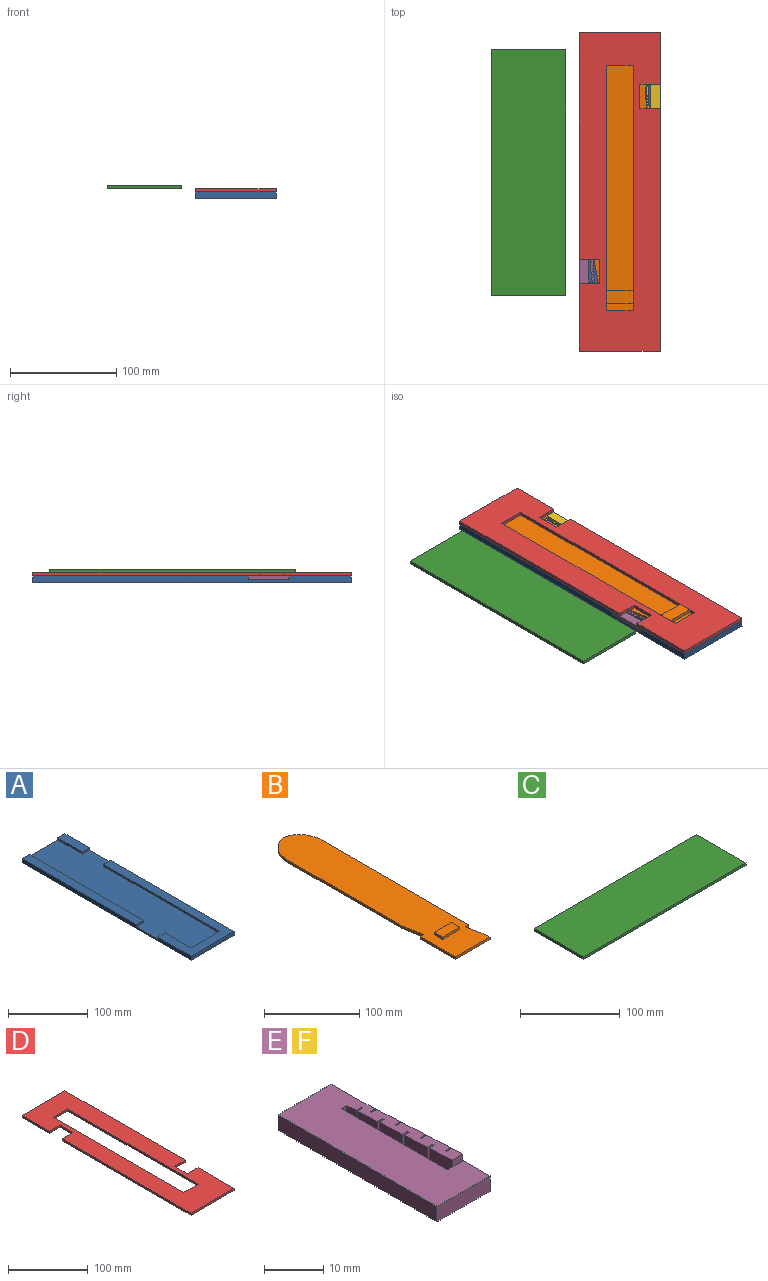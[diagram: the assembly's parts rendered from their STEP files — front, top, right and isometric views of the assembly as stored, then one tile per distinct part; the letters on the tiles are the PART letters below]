
ASSEMBLY  parts=6 mates=5
PART A: 18 faces, bbox 76.2x299.7x6.4 mm
  f0: plane 43.39x12.7mm, normal (0,0,1), area 551.1mm2, adj f7,f9,f16,f17
  f1: plane 205.53x3.18mm, normal (-1,0,0), area 652.6mm2, adj f3,f6,f10,f15
  f2: plane 202.95x3.18mm, normal (1,0,0), area 644.4mm2, adj f6,f12,f13,f17
  f3: plane 218.23x76.2mm, normal (0,0,1), area 4161.8mm2, adj f1,f4,f5,f7,f10,f11,f14,f15
  f4: plane 299.72x6.35mm, normal (-1,0,0), area 1782.3mm2, adj f3,f5,f6,f8,f12,f13,f14,f17
  f5: plane 76.2x6.35mm, normal (0,-1,0), area 483.9mm2, adj f3,f4,f7,f8
  f6: plane 287.02x76.2mm, normal (0,0,1), area 15548.4mm2, adj f1,f2,f4,f7,f9,f10,f11,f13
  f7: plane 299.72x6.35mm, normal (1,0,0), area 1782.3mm2, adj f0,f3,f5,f6,f8,f15,f16,f17
  f8: plane 299.72x76.2mm, normal (0,0,-1), area 22838.7mm2, adj f4,f5,f7,f17
  f9: plane 43.39x3.18mm, normal (-1,0,0), area 137.8mm2, adj f0,f6,f16,f17
  f10: plane 50.8x3.18mm, normal (0,1,0), area 161.3mm2, adj f1,f3,f6,f11
  f11: plane 45.97x3.18mm, normal (1,0,0), area 146mm2, adj f3,f6,f10,f14
  f12: plane 202.95x12.7mm, normal (0,0,1), area 2577.4mm2, adj f2,f4,f13,f17
  f13: plane 12.7x3.18mm, normal (0,-1,0), area 40.3mm2, adj f2,f4,f6,f12
  f14: plane 12.7x3.18mm, normal (0,1,0), area 40.3mm2, adj f3,f4,f6,f11
  f15: plane 12.7x3.18mm, normal (0,1,0), area 40.3mm2, adj f1,f3,f6,f7
  f16: plane 12.7x3.18mm, normal (0,-1,0), area 40.3mm2, adj f0,f6,f7,f9
  f17: plane 76.2x6.35mm, normal (0,1,0), area 322.6mm2, adj f0,f2,f4,f6,f7,f8,f9,f12
PART B: 20 faces, bbox 50.8x281.3x6.4 mm
  f0: plane 171.2x3.18mm, normal (-1,0,0), area 543.5mm2, adj f2,f6,f8,f18
  f1: plane 6.14x3.18mm, normal (1,0,0), area 19.5mm2, adj f2,f4,f8,f19
  f2: plane 281.3x50.8mm, normal (0,0,1), area 13440.3mm2, adj f0,f1,f3,f4,f5,f6,f7,f9
  f3: plane 218.65x3.18mm, normal (1,0,0), area 694.2mm2, adj f2,f7,f8,f14
  f4: plane 50.8x3.18mm, normal (0,-1,0), area 161.3mm2, adj f1,f2,f5,f8
  f5: plane 52.32x3.18mm, normal (-1,0,0), area 166.1mm2, adj f2,f4,f8,f15
  f6: cylinder r=31.75mm len=31.11mm, axis (0,0,1), area 138mm2, adj f0,f2,f7,f8
  f7: cylinder r=31.75mm len=31.11mm, axis (0,0,1), area 138mm2, adj f2,f3,f6,f8
  f8: plane 281.3x50.8mm, normal (0,0,-1), area 13762.9mm2, adj f0,f1,f3,f4,f5,f6,f7,f14
  f9: plane 12.7x3.18mm, normal (-1,0,0), area 40.3mm2, adj f2,f10,f12,f13
  f10: plane 25.4x3.18mm, normal (0,-1,0), area 80.6mm2, adj f2,f9,f11,f13
  f11: plane 12.7x3.18mm, normal (1,0,0), area 40.3mm2, adj f2,f10,f12,f13
  f12: plane 25.4x3.18mm, normal (0,1,0), area 80.6mm2, adj f2,f9,f11,f13
  f13: plane 25.4x12.7mm, normal (0,0,1), area 322.6mm2, adj f9,f10,f11,f12
  f14: plane 5.08x3.18mm, normal (0,-1,0), area 16.1mm2, adj f2,f3,f8,f16
  f15: plane 5.08x3.18mm, normal (0,1,0), area 16.1mm2, adj f2,f5,f8,f17
  f16: plane 24.38x4.98mm, normal (0.98,0.2,0), area 79mm2, adj f2,f8,f14,f19
  f17: plane 25.7x4.99mm, normal (-0.98,-0.19,0), area 83.1mm2, adj f2,f8,f15,f18
  f18: cylinder r=5.08mm len=3.18mm, axis (0,0,1), area 3.1mm2, adj f0,f2,f8,f17
  f19: cylinder r=5.08mm len=3.18mm, axis (0,0,1), area 3.2mm2, adj f1,f2,f8,f16
PART C: 6 faces, bbox 231.1x69.9x3.2 mm
  f0: plane 69.85x3.18mm, normal (-1,0,0), area 221.8mm2, adj f1,f3,f4,f5
  f1: plane 231.14x3.18mm, normal (0,-1,0), area 733.9mm2, adj f0,f2,f4,f5
  f2: plane 69.85x3.18mm, normal (1,0,0), area 221.8mm2, adj f1,f3,f4,f5
  f3: plane 231.14x3.18mm, normal (0,1,0), area 733.9mm2, adj f0,f2,f4,f5
  f4: plane 231.14x69.85mm, normal (0,0,1), area 16145.1mm2, adj f0,f1,f2,f3
  f5: plane 231.14x69.85mm, normal (0,0,-1), area 16145.1mm2, adj f0,f1,f2,f3
PART D: 18 faces, bbox 76.2x299.7x3.2 mm
  f0: plane 299.72x76.2mm, normal (0,0,1), area 16096.7mm2, adj f2,f3,f4,f5,f6,f7,f8,f9
  f1: plane 299.72x76.2mm, normal (0,0,-1), area 16096.7mm2, adj f2,f3,f4,f5,f6,f7,f8,f9
  f2: plane 22.86x3.18mm, normal (-1,0,0), area 72.6mm2, adj f0,f1,f15,f16
  f3: plane 22.86x3.18mm, normal (1,0,0), area 72.6mm2, adj f0,f1,f13,f14
  f4: plane 231.14x3.18mm, normal (1,0,0), area 733.9mm2, adj f0,f1,f5,f7
  f5: plane 25.4x3.18mm, normal (0,-1,0), area 80.6mm2, adj f0,f1,f4,f6
  f6: plane 231.14x3.18mm, normal (-1,0,0), area 733.9mm2, adj f0,f1,f5,f7
  f7: plane 25.4x3.18mm, normal (0,1,0), area 80.6mm2, adj f0,f1,f4,f6
  f8: plane 213.11x3.18mm, normal (1,0,0), area 676.6mm2, adj f0,f1,f13,f17
  f9: plane 48.51x3.18mm, normal (-1,0,0), area 154mm2, adj f0,f1,f15,f17
  f10: plane 63.75x3.18mm, normal (1,0,0), area 202.4mm2, adj f0,f1,f12,f14
  f11: plane 228.35x3.18mm, normal (-1,0,0), area 725mm2, adj f0,f1,f12,f16
  f12: plane 76.2x3.18mm, normal (0,-1,0), area 241.9mm2, adj f0,f1,f10,f11
  f13: plane 19.05x3.18mm, normal (0,-1,0), area 60.5mm2, adj f0,f1,f3,f8
  f14: plane 19.05x3.18mm, normal (0,1,0), area 60.5mm2, adj f0,f1,f3,f10
  f15: plane 19.05x3.18mm, normal (0,-1,0), area 60.5mm2, adj f0,f1,f2,f9
  f16: plane 19.05x3.18mm, normal (0,1,0), area 60.5mm2, adj f0,f1,f2,f11
  f17: plane 76.2x3.18mm, normal (0,1,0), area 241.9mm2, adj f0,f1,f8,f9
PART E: 45 faces, bbox 14x38.1x3.2 mm
  f0: plane 5.38x3.18mm, normal (1,0.05,0), area 17.1mm2, adj f8,f9,f34,f41
  f1: plane 5.38x3.18mm, normal (1,0.05,0), area 17.1mm2, adj f8,f9,f29,f35
  f2: plane 4.06x3.18mm, normal (1,0.05,0), area 12.9mm2, adj f8,f9,f14,f27
  f3: plane 5.38x3.18mm, normal (1,0.05,0), area 17.1mm2, adj f8,f9,f21,f40
  f4: plane 5.38x3.18mm, normal (-1,-0.05,0), area 17.1mm2, adj f8,f9,f12,f44
  f5: plane 5.38x3.18mm, normal (-1,-0.05,0), area 17.1mm2, adj f8,f9,f36,f43
  f6: plane 4.64x3.18mm, normal (-1,-0.05,0), area 14.7mm2, adj f8,f9,f26,f32
  f7: plane 5.38x3.18mm, normal (-1,-0.05,0), area 17.1mm2, adj f8,f9,f24,f38
  f8: plane 38.1x14.01mm, normal (0,0,1), area 445.1mm2, adj f0,f1,f2,f3,f4,f5,f6,f7
  f9: plane 38.1x14.01mm, normal (0,0,-1), area 445.1mm2, adj f0,f1,f2,f3,f4,f5,f6,f7
  f10: plane 3.18x1.27mm, normal (0,-1,0), area 4mm2, adj f8,f9,f11,f20
  f11: plane 3.18x2.1mm, normal (-1,-0.05,0), area 6.7mm2, adj f8,f9,f10,f31
  f12: plane 3.18x2.54mm, normal (0.05,-1,0), area 8.1mm2, adj f4,f8,f9,f13
  f13: plane 3.18x2.54mm, normal (1,0.05,0), area 8.1mm2, adj f8,f9,f12,f23
  f14: plane 6.35x3.18mm, normal (1,0,0), area 20.2mm2, adj f2,f8,f9,f15
  f15: plane 12.7x3.18mm, normal (0,1,0), area 40.3mm2, adj f8,f9,f14,f16
  f16: plane 38.1x3.18mm, normal (-1,0,0), area 121mm2, adj f8,f9,f15,f17
  f17: plane 12.7x3.18mm, normal (0,-1,0), area 40.3mm2, adj f8,f9,f16,f18
  f18: plane 6.35x3.18mm, normal (1,0,0), area 20.2mm2, adj f8,f9,f17,f19
  f19: plane 3.81x3.18mm, normal (0,1,0), area 12.1mm2, adj f8,f9,f18,f20
  f20: plane 25.4x3.18mm, normal (1,0,0), area 80.6mm2, adj f8,f9,f10,f19
  f21: plane 3.18x1.27mm, normal (0.05,-1,0), area 4mm2, adj f3,f8,f9,f22
  f22: plane 3.18x0.3mm, normal (1,0.05,0), area 1mm2, adj f8,f9,f21,f23
  f23: plane 3.18x1.27mm, normal (-0.05,1,0), area 4mm2, adj f8,f9,f13,f22
  f24: plane 3.18x1.27mm, normal (-0.05,1,0), area 4mm2, adj f7,f8,f9,f25
  f25: plane 3.18x0.3mm, normal (-1,-0.05,0), area 1mm2, adj f8,f9,f24,f26
  f26: plane 3.18x1.27mm, normal (0.05,-1,0), area 4mm2, adj f6,f8,f9,f25
  f27: plane 3.18x1.27mm, normal (0.05,-1,0), area 4mm2, adj f2,f8,f9,f28
  f28: plane 3.18x0.3mm, normal (1,0.05,0), area 1mm2, adj f8,f9,f27,f29
  f29: plane 3.18x1.27mm, normal (-0.05,1,0), area 4mm2, adj f1,f8,f9,f28
  f30: plane 3.18x0.3mm, normal (-1,-0.05,0), area 1mm2, adj f8,f9,f31,f32
  f31: plane 3.18x1.27mm, normal (0.05,-1,0), area 4mm2, adj f8,f9,f11,f30
  f32: plane 3.18x1.27mm, normal (-0.05,1,0), area 4mm2, adj f6,f8,f9,f30
  f33: plane 3.18x0.3mm, normal (1,0.05,0), area 1mm2, adj f8,f9,f34,f35
  f34: plane 3.18x1.27mm, normal (-0.05,1,0), area 4mm2, adj f0,f8,f9,f33
  f35: plane 3.18x1.27mm, normal (0.05,-1,0), area 4mm2, adj f1,f8,f9,f33
  f36: plane 3.18x1.27mm, normal (-0.05,1,0), area 4mm2, adj f5,f8,f9,f37
  f37: plane 3.18x0.3mm, normal (-1,-0.05,0), area 1mm2, adj f8,f9,f36,f38
  f38: plane 3.18x1.27mm, normal (0.05,-1,0), area 4mm2, adj f7,f8,f9,f37
  f39: plane 3.18x0.3mm, normal (1,0.05,0), area 1mm2, adj f8,f9,f40,f41
  f40: plane 3.18x1.27mm, normal (-0.05,1,0), area 4mm2, adj f3,f8,f9,f39
  f41: plane 3.18x1.27mm, normal (0.05,-1,0), area 4mm2, adj f0,f8,f9,f39
  f42: plane 3.18x0.3mm, normal (-1,-0.05,0), area 1mm2, adj f8,f9,f43,f44
  f43: plane 3.18x1.27mm, normal (0.05,-1,0), area 4mm2, adj f5,f8,f9,f42
  f44: plane 3.18x1.27mm, normal (-0.05,1,0), area 4mm2, adj f4,f8,f9,f42
PART F: same geometry as E
PLACE A t=(-114.36,-316.76,-337.25)mm fixed
PLACE B t=(-139.76,-236.62,-337.25)mm
PLACE C rot(axis=(0,0,-1),90deg) t=(-168.21,-115.6,-327.73)mm
PLACE D rot(axis=(0,1,0),180deg) t=(-60.39,-233.57,-327.73)mm
PLACE E t=(-114.36,-258.08,-334.08)mm
PLACE F rot(axis=(0,0,-1),180deg) t=(-38.16,-60.43,-334.08)mm
MATE fastened E.f15 <-> A.f13  axis (0,1,0) through (-108.01,-219.98,-332.49)mm
MATE fastened F.f15 <-> A.f15  axis (0,-1,0) through (-44.51,-98.53,-332.49)mm
MATE slider A.f10 <-> B.f4  axis (0,1,0) through (-76.26,-304.06,-332.49)mm
MATE planar C.f5 <-> D.f1  axis (0,0,-1) through (-161.86,-148.62,-327.73)mm
MATE fastened A.f3 <-> D.f0  axis (0,0,1) through (-76.26,-316.76,-330.9)mm
